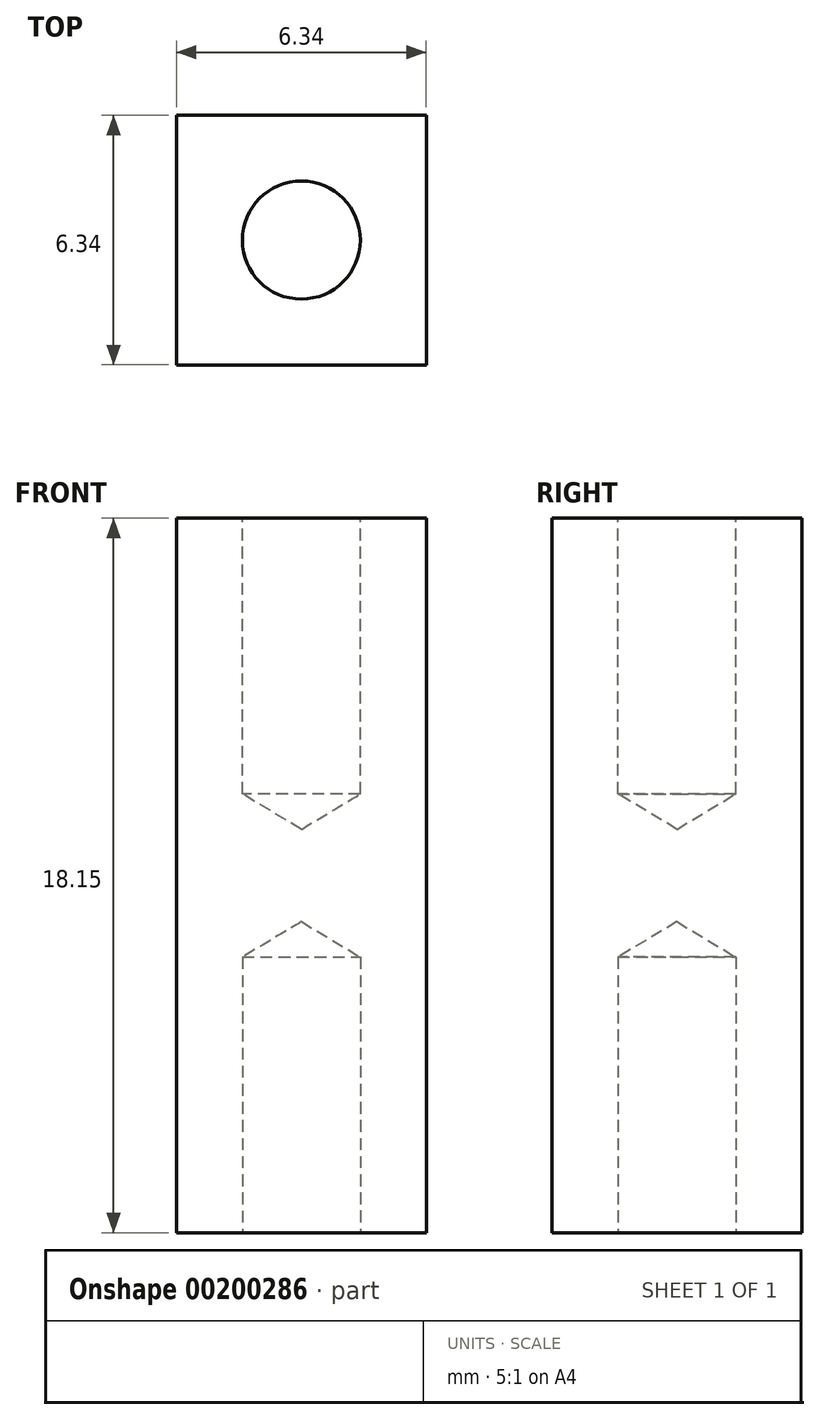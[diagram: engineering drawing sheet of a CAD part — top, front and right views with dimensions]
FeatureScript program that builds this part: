
annotation { "Feature Type Name" : "Feature", "Feature Type Description" : "" }
export const myFeature = defineFeature(function(context is Context, id is Id, definition is map)
    precondition{}
    {
        {
            var Q0;
            Q0=qCreatedBy(makeId("Top.planeOp"),FACE);
            var sketch = newSketch(context, id + "F0", { "sketchPlane" : qUnion([Q0])});
            skLineSegment(sketch, "E0.bottom", {"start": v(3.18, -3.18) * mm, "end": v(-3.17, -3.18) * mm});
            skLineSegment(sketch, "E0.top", {"start": v(3.17, 3.18) * mm, "end": v(-3.18, 3.17) * mm});
            skLineSegment(sketch, "E0.left", {"start": v(3.18, -3.18) * mm, "end": v(3.17, 3.18) * mm});
            skLineSegment(sketch, "E0.right", {"start": v(-3.17, -3.18) * mm, "end": v(-3.18, 3.17) * mm});
            skPoint(sketch, "E0.middle", {"position": v(0, 0) * mm});
            skSolve(sketch);
        }
        {
            var Q0;
            Q0 = qSketchRegion(id + "F0", true);
            extrude(context, id + "F1", {"entities" : qUnion([Q0]), "depth" : 18.15 * mm, "offsetDistance" : 25 * mm});
        }
        {
            var Q0;
            Q0=sQuery(id+"F0.wireOp",VERTEX,"E0.middle");
            var Q1;
            Q1=makeQuery(id+"F1.opExtrude","SWEPT_BODY",BODY,{"disambiguationData":[OSD([sQuery(id+"F0.wireOp",EDGE,"E0.bottom"),sQuery(id+"F0.wireOp",EDGE,"E0.top"),sQuery(id+"F0.wireOp",EDGE,"E0.left"),sQuery(id+"F0.wireOp",EDGE,"E0.right")])]});
            hole(context, id + "F2", {"style" : HoleStyle.SIMPLE, "endStyle" : HoleEndStyle.BLIND, "oppositeDirection" : true, "standardTappedOrClearance" : lookupTablePath({ "standard" : "ISO", "size" : "3", "type" : "Drilled" }), "standardBlindInLast" : lookupTablePath({ "standard" : "ISO", "size" : "3", "type" : "Drilled" }), "holeDiameter" : 3 * mm, "holeDepth" : 7 * mm, "startFromSketch" : true, "locations" : qUnion([Q0]), "scope" : qUnion([Q1])});
        }
        {
            var Q0;
            Q0=makeQuery(id+"F1.opExtrude","CAP_FACE",FACE,{"disambiguationData":[OSD([sQuery(id+"F0.wireOp",EDGE,"E0.bottom"),sQuery(id+"F0.wireOp",EDGE,"E0.top"),sQuery(id+"F0.wireOp",EDGE,"E0.left"),sQuery(id+"F0.wireOp",EDGE,"E0.right")])],"isStart":false});
            var sketch = newSketch(context, id + "F3", { "sketchPlane" : qUnion([Q0])});
            skPoint(sketch, "E1", {"position": v(0, 0) * mm});
            skSolve(sketch);
        }
        {
            var Q0;
            Q0=sQuery(id+"F3.wireOp",VERTEX,"E1");
            var Q1;
            Q1=makeQuery(id+"F1.opExtrude","SWEPT_BODY",BODY,{"disambiguationData":[OSD([sQuery(id+"F0.wireOp",EDGE,"E0.bottom"),sQuery(id+"F0.wireOp",EDGE,"E0.top"),sQuery(id+"F0.wireOp",EDGE,"E0.left"),sQuery(id+"F0.wireOp",EDGE,"E0.right")])]});
            hole(context, id + "F4", {"style" : HoleStyle.SIMPLE, "endStyle" : HoleEndStyle.BLIND, "standardTappedOrClearance" : lookupTablePath({ "standard" : "ISO", "size" : "3", "type" : "Drilled" }), "standardBlindInLast" : lookupTablePath({ "standard" : "ISO", "size" : "3", "type" : "Drilled" }), "holeDiameter" : 3 * mm, "holeDepth" : 7 * mm, "startFromSketch" : true, "locations" : qUnion([Q0]), "scope" : qUnion([Q1])});
        }
    });
